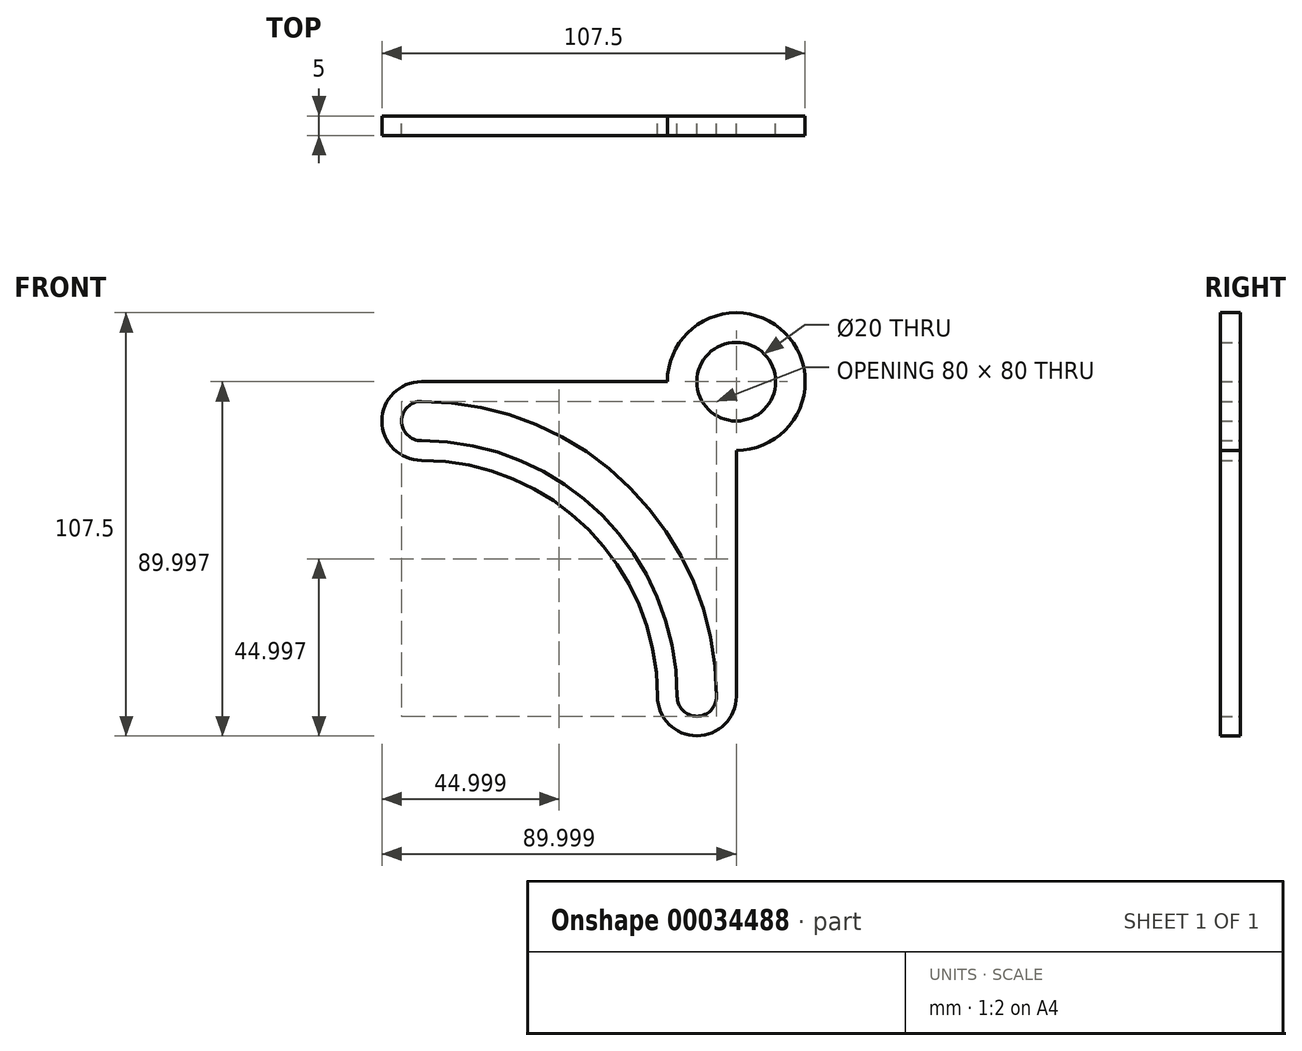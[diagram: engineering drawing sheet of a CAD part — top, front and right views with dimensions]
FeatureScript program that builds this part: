
annotation { "Feature Type Name" : "Feature", "Feature Type Description" : "" }
export const myFeature = defineFeature(function(context is Context, id is Id, definition is map)
    precondition{}
    {
        {
            var Q0;
            Q0=qCreatedBy(makeId("Front.planeOp"),FACE);
            var sketch = newSketch(context, id + "F0", { "sketchPlane" : qUnion([Q0])});
            skCircle(sketch, "E0", {"center": v(22.27, 23.17) * mm, "radius": 17.5 * mm});
            skCircle(sketch, "E1", {"center": v(22.27, 23.17) * mm, "radius": 10 * mm});
            skLineSegment(sketch, "E2.bottom", {"start": v(22.27, 23.17) * mm, "end": v(-57.73, 23.17) * mm});
            skLineSegment(sketch, "E2.top", {"start": v(22.27, -56.83) * mm, "end": v(-57.73, -56.83) * mm});
            skLineSegment(sketch, "E2.left", {"start": v(22.27, 23.17) * mm, "end": v(22.27, -56.83) * mm});
            skLineSegment(sketch, "E2.right", {"start": v(-57.73, 23.17) * mm, "end": v(-57.73, -56.83) * mm});
            skCircle(sketch, "E3", {"center": v(-57.73, 13.17) * mm, "radius": 10 * mm});
            skCircle(sketch, "E4", {"center": v(-57.73, 13.17) * mm, "radius": 5 * mm});
            skCircle(sketch, "E5", {"center": v(12.27, -56.83) * mm, "radius": 10 * mm});
            skCircle(sketch, "E6", {"center": v(12.27, -56.83) * mm, "radius": 5 * mm});
            skArc(sketch, "E7", {"start": v(7.27, -56.83) * mm, "mid": v(-11.77, -10.87) * mm, "end": v(-57.73, 8.17) * mm});
            skArc(sketch, "E8", {"start": v(17.27, -56.83) * mm, "mid": v(-4.7, -3.8) * mm, "end": v(-57.73, 18.17) * mm});
            skArc(sketch, "E9", {"start": v(2.27, -56.83) * mm, "mid": v(-15.3, -14.4) * mm, "end": v(-57.73, 3.17) * mm});
            skSolve(sketch);
        }
        {
            var Q0;
            {var subQ7=sQuery(id+"F0.wireOp",EDGE,"E2.bottom");var subQ9=sQuery(id+"F0.wireOp",EDGE,"E0");var subQ11=makeQuery(id+"F0.imprint","INTERSECT",VERTEX,{"derivedFrom":[subQ9,subQ7]});Q0=makeQuery(id+"F0.imprint","IMPRINT",FACE,{"disambiguationData":[TD([[makeQuery(id+"F0.imprint","IMPRINT",EDGE,{"disambiguationData":[TD([[subQ11,-1.0]])],"derivedFrom":subQ9}),-1.0]])]});}
            var Q1;
            {var subQ0=sQuery(id+"F0.wireOp",EDGE,"E9");Q1=makeQuery(id+"F0.imprint","IMPRINT",FACE,{"disambiguationData":[TD([[makeQuery(id+"F0.imprint","IMPRINT",EDGE,{"derivedFrom":subQ0}),-1.0]])]});}
            var Q2;
            {var subQ0=sQuery(id+"F0.wireOp",EDGE,"E7");var subQ1=sQuery(id+"F0.wireOp",EDGE,"E5");var subQ2=makeQuery(id+"F0.imprint","INTERSECT",VERTEX,{"derivedFrom":[subQ1,subQ0]});Q2=makeQuery(id+"F0.imprint","IMPRINT",FACE,{"disambiguationData":[TD([[makeQuery(id+"F0.imprint","IMPRINT",EDGE,{"disambiguationData":[TD([[subQ2,-1.0]])],"derivedFrom":subQ1}),1.0]])]});}
            var Q3;
            {var subQ1=sQuery(id+"F0.wireOp",EDGE,"E2.top");var subQ4=sQuery(id+"F0.wireOp",EDGE,"E5");var subQ6=makeQuery(id+"F0.imprint","INTERSECT",VERTEX,{"derivedFrom":[subQ1,sQuery(id+"F0.wireOp",EDGE,"E2.left"),subQ4]});Q3=makeQuery(id+"F0.imprint","IMPRINT",FACE,{"disambiguationData":[TD([[makeQuery(id+"F0.imprint","IMPRINT",EDGE,{"disambiguationData":[TD([[subQ6,-1.0]])],"derivedFrom":subQ1}),1.0]])]});}
            var Q4;
            {var subQ0=sQuery(id+"F0.wireOp",EDGE,"E8");var subQ1=sQuery(id+"F0.wireOp",EDGE,"E5");var subQ2=makeQuery(id+"F0.imprint","INTERSECT",VERTEX,{"derivedFrom":[subQ1,subQ0]});Q4=makeQuery(id+"F0.imprint","IMPRINT",FACE,{"disambiguationData":[TD([[makeQuery(id+"F0.imprint","IMPRINT",EDGE,{"disambiguationData":[TD([[subQ2,1.0]])],"derivedFrom":subQ1}),1.0]])]});}
            var Q5;
            {var subQ1=sQuery(id+"F0.wireOp",EDGE,"E2.right");var subQ4=sQuery(id+"F0.wireOp",EDGE,"E3");var subQ6=makeQuery(id+"F0.imprint","INTERSECT",VERTEX,{"derivedFrom":[sQuery(id+"F0.wireOp",EDGE,"E2.bottom"),subQ1,subQ4]});Q5=makeQuery(id+"F0.imprint","IMPRINT",FACE,{"disambiguationData":[TD([[makeQuery(id+"F0.imprint","IMPRINT",EDGE,{"disambiguationData":[TD([[subQ6,-1.0]])],"derivedFrom":subQ1}),-1.0]])]});}
            var Q6;
            {var subQ0=sQuery(id+"F0.wireOp",EDGE,"E8");var subQ1=sQuery(id+"F0.wireOp",EDGE,"E3");var subQ2=makeQuery(id+"F0.imprint","INTERSECT",VERTEX,{"derivedFrom":[subQ1,subQ0]});Q6=makeQuery(id+"F0.imprint","IMPRINT",FACE,{"disambiguationData":[TD([[makeQuery(id+"F0.imprint","IMPRINT",EDGE,{"disambiguationData":[TD([[subQ2,-1.0]])],"derivedFrom":subQ1}),1.0]])]});}
            var Q7;
            {var subQ0=sQuery(id+"F0.wireOp",EDGE,"E7");var subQ1=sQuery(id+"F0.wireOp",EDGE,"E3");var subQ2=makeQuery(id+"F0.imprint","INTERSECT",VERTEX,{"derivedFrom":[subQ1,subQ0]});Q7=makeQuery(id+"F0.imprint","IMPRINT",FACE,{"disambiguationData":[TD([[makeQuery(id+"F0.imprint","IMPRINT",EDGE,{"disambiguationData":[TD([[subQ2,1.0]])],"derivedFrom":subQ1}),1.0]])]});}
            var Q8;
            {var subQ3=sQuery(id+"F0.wireOp",EDGE,"E0");var subQ5=sQuery(id+"F0.wireOp",EDGE,"E2.bottom");var subQ7=makeQuery(id+"F0.imprint","INTERSECT",VERTEX,{"derivedFrom":[subQ3,subQ5]});Q8=makeQuery(id+"F0.imprint","IMPRINT",FACE,{"disambiguationData":[TD([[makeQuery(id+"F0.imprint","IMPRINT",EDGE,{"disambiguationData":[TD([[subQ7,-1.0]])],"derivedFrom":subQ3}),1.0]])]});}
            var Q9;
            {var subQ0=sQuery(id+"F0.wireOp",EDGE,"E2.bottom");var subQ3=sQuery(id+"F0.wireOp",EDGE,"E0");var subQ4=makeQuery(id+"F0.imprint","INTERSECT",VERTEX,{"derivedFrom":[subQ3,subQ0]});Q9=makeQuery(id+"F0.imprint","IMPRINT",FACE,{"disambiguationData":[TD([[makeQuery(id+"F0.imprint","IMPRINT",EDGE,{"disambiguationData":[TD([[subQ4,1.0]])],"derivedFrom":subQ3}),1.0]])]});}
            extrude(context, id + "F1", {"entities" : qUnion([Q0, Q1, Q2, Q3, Q4, Q5, Q6, Q7, Q8, Q9]), "depth" : 5 * mm});
        }
    });
